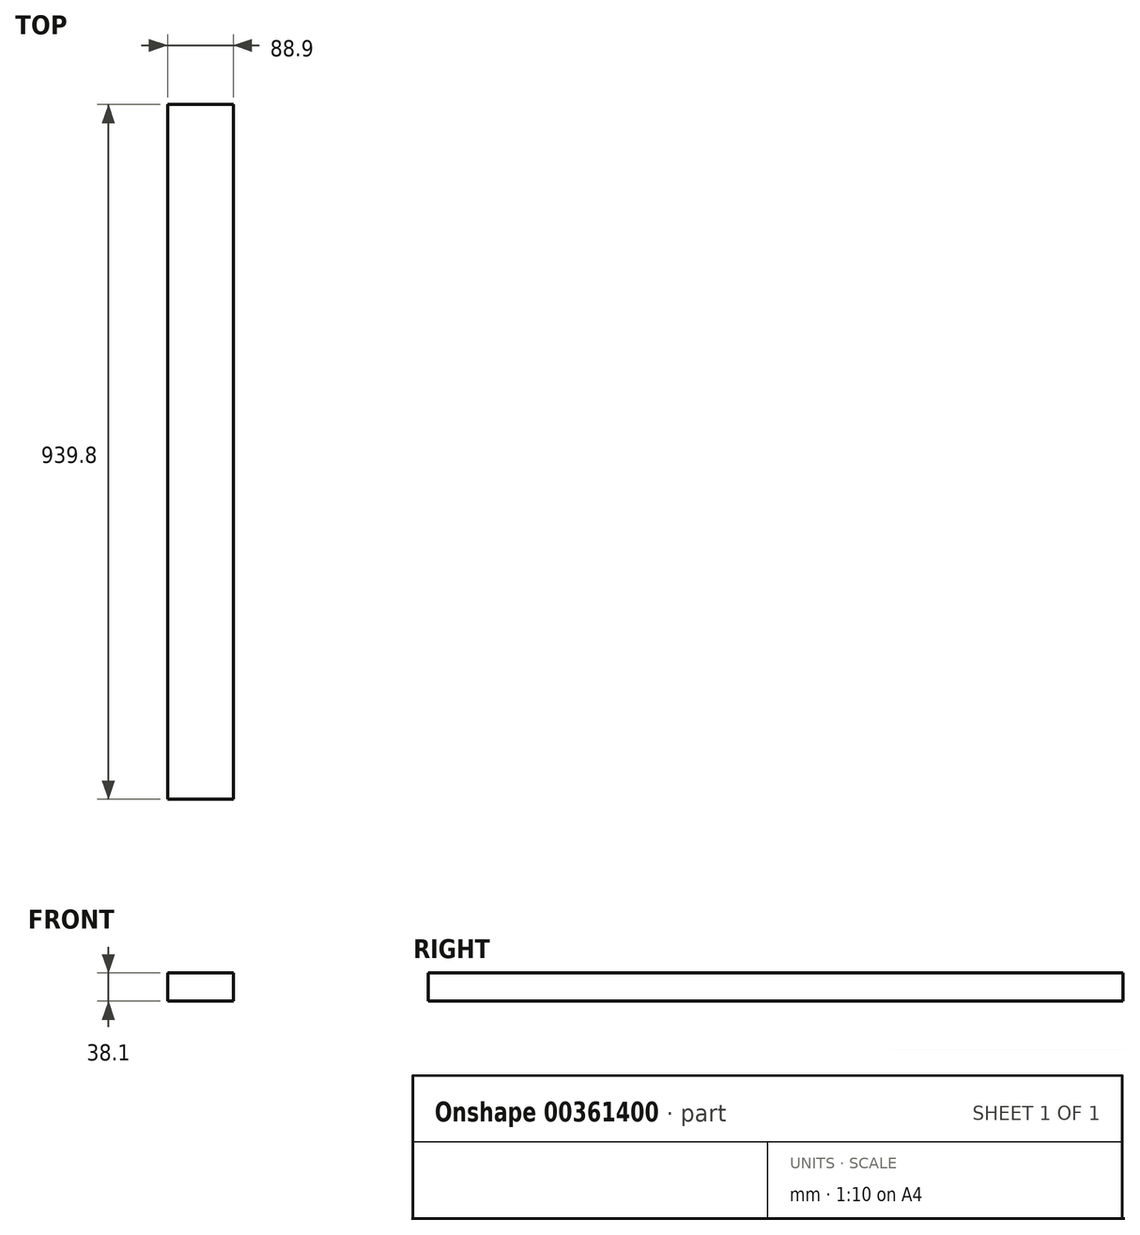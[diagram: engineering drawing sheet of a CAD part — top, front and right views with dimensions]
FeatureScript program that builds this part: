
annotation { "Feature Type Name" : "Feature", "Feature Type Description" : "" }
export const myFeature = defineFeature(function(context is Context, id is Id, definition is map)
    precondition{}
    {
        {
            var Q0;
            Q0=qCreatedBy(makeId("Front.planeOp"),FACE);
            var sketch = newSketch(context, id + "F0", { "sketchPlane" : qUnion([Q0])});
            skLineSegment(sketch, "E0.bottom", {"start": v(0, 0) * mm, "end": v(88.9, 0) * mm});
            skLineSegment(sketch, "E0.top", {"start": v(0, 38.1) * mm, "end": v(88.9, 38.1) * mm});
            skLineSegment(sketch, "E0.left", {"start": v(0, 0) * mm, "end": v(0, 38.1) * mm});
            skLineSegment(sketch, "E0.right", {"start": v(88.9, 0) * mm, "end": v(88.9, 38.1) * mm});
            skSolve(sketch);
        }
        {
            var Q0;
            Q0=makeQuery(id+"F0.imprint","IMPRINT",FACE,{"disambiguationData":[TD([[makeQuery(id+"F0.imprint","IMPRINT",EDGE,{"derivedFrom":sQuery(id+"F0.wireOp",EDGE,"E0.bottom")}),1.0]])]});
            extrude(context, id + "F1", {"entities" : qUnion([Q0]), "flatOperationType" : FlatOperationType.REMOVE, "oppositeDirection" : true, "offsetDistance" : 25.4 * mm, "depth" : 939.8 * mm, "domain" : OperationDomain.MODEL});
        }
    });
